# Revit family: KDW030059
name_source: partatom
category: Plumbing Fixtures
revit_build: Autodesk Revit 2015 (Build: 20140606_1530(x64)
units: mm (PartAtom-declared; Revit-internal decimal feet)

## types (1)
- KDW030059
    Additional features of the object = https://www.kaldewei.co.uk
    BIMobject category = Basins
    Brand url = http://www.kaldewei.com
    Color = https://www.kaldewei.co.uk
    ColourOptions = https://www.kaldewei.co.uk
    Configurator link = https://www.kaldewei.co.uk
    Description details = KALDEWEI international Worldwide partner for iconic bathroom solutions made of KALDEWEI steel enamel  KALDEWEI steel enamel delivers unique advantages that inspire excellence in bathroom design. Projects across the world, from upmarket hotels to private homes, capture the sophisticated aesthetic that recommends KALDEWEI as the partner of choice. As a leading international manufacturer of high-quality shower surfaces, bathtubs and washbasins made of superior steel enamel, KALDEWEI today is present in more than 80 countries.
    Design country = Germany
    Durability = https://EN 14688
    Edition number = 1
    Finish = Kaldewei
    IFC Classification = Furnishing Element
    IfcExportAs = WASHHANDBASIN
    IfcExportType = IfcSanitaryTerminalType
    Link towards a photo of the product = https://www.kaldewei.co.uk
    Manufacturer country = Germany
    ManufacturerCountry = GERMANY
    ManufacturerName = KALDEWEI
    Material = steel enamel
    Material main = Steel
    Material secondary = Enamel
    NBS Reference Code = 35-65-70-94
    NBS Reference Description = Wash Basin Systems
    Name = CONO Undercounter washbasin
    Nominal height = 470 cm
    Nominal width = 380 cm
    ObjectName = CONO Undercounter washbasin
    ObjectNorm = EN 14688 EU DECLARATION OF PERFORMANCE (https://www.kaldewei.de
    Polantis code = KDW030059
    Product Guid = a5c92beb-e71c-4b7b-a28b-e8171dee1915
    Product SKU = 3078
    Product certification = https://www.kaldewei.co.uk
    Product data url = https://bimobject.com
    Product family = CONO
    Product group = Washbasin
    Product url = https://www.kaldewei.co.uk
    ProductInformation = Model No. 3078: The formal clarity and tranquillity of the CONO washbasins are a fusion of aesthetic and user-friendliness. This applies to an even greater extent to the new square model which, thanks to its compact dimensions, fits perfectly where other versions appear out of proportion. What makes this CONO washbasin an especially practical solution is that it can be installed in every conceivable way and is available with 1, 3 or no tap holes.
    QR code = http://bimobject.com
    SerialNumber = 3078
    Shape = Undercounter
    Size = 380x470
    Sound Insulation = DIN 4109:2016, VDI4100:2012
    Sustainability = https://EN 15804
    Technical data link = https://kaldewei.typo-live.web-factory.de
    Technical description = https://www.kaldewei.co.uk
    Type of accessories = https://www.kaldewei.co.uk
    Type of support framing = https://www.kaldewei.co.uk
    UNSPSC Code = 301815
    UNSPSCCode = 30181504
    UNSPSCNames = Sinks
    URL = https://www.kaldewei.com
    Uniclass 1.4 Code = L7212
    Uniclass 1.4 Description = Washbasins
    Uniclass 2.0 Code = SS-35-65-70-94
    Uniclass 2.0 Description = Wash Basin Systems
    Uniclass2 = Pr_40_20_96
    Version = 3
    WarrantyDurationParts = 30
    WarrantyDurationUnit = Year
    WarrantyStartDate = https://www.kaldewei.co.uk
    Website link = https://www.kaldewei.co.uk
    Weight = 4.5
    Weight Net (Kg) = 4.5

## geometry (parser evidence)
native form markers: Sweep x6
no freeform markers — native parametric forms only
